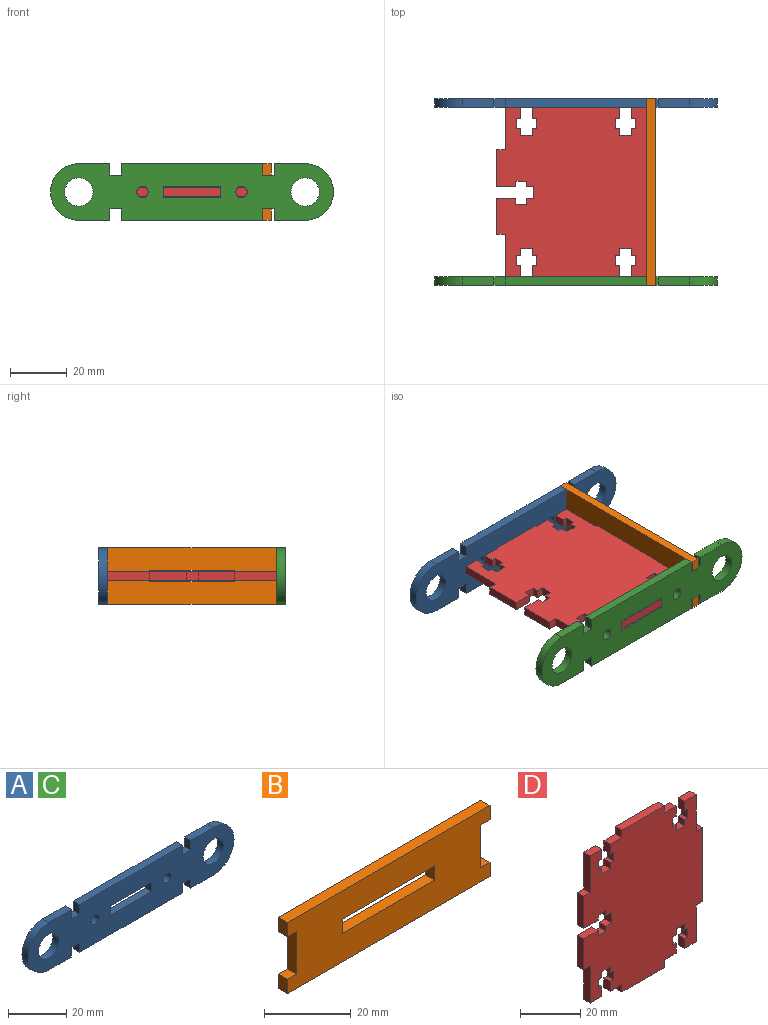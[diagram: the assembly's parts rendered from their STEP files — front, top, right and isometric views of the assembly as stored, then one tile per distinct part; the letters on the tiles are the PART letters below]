
ASSEMBLY  parts=4 mates=7
PART A: 30 faces, bbox 100x3x20 mm
  f0: cylinder r=10mm len=20mm, axis (0,1,0), area 94.2mm2, adj f1,f23,f28,f29
  f1: plane 11x3mm, normal (0,0,1), area 33mm2, adj f0,f2,f28,f29
  f2: plane 4x3mm, normal (-1,0,0), area 12mm2, adj f1,f3,f28,f29
  f3: plane 4x3mm, normal (0,0,1), area 12mm2, adj f2,f4,f28,f29
  f4: plane 4x3mm, normal (1,0,0), area 12mm2, adj f3,f5,f28,f29
  f5: plane 50x3mm, normal (0,0,1), area 150mm2, adj f4,f6,f28,f29
  f6: plane 4x3mm, normal (-1,0,0), area 12mm2, adj f5,f7,f28,f29
  f7: plane 4x3mm, normal (0,0,1), area 12mm2, adj f6,f8,f28,f29
  f8: plane 4x3mm, normal (1,0,0), area 12mm2, adj f7,f9,f28,f29
  f9: plane 11x3mm, normal (0,0,1), area 33mm2, adj f8,f10,f28,f29
  f10: cylinder r=10mm len=20mm, axis (0,1,0), area 94.2mm2, adj f9,f11,f28,f29
  f11: plane 11x3mm, normal (0,0,-1), area 33mm2, adj f10,f12,f28,f29
  f12: plane 4x3mm, normal (1,0,0), area 12mm2, adj f11,f13,f28,f29
  f13: plane 4x3mm, normal (0,0,-1), area 12mm2, adj f12,f14,f28,f29
  f14: plane 4x3mm, normal (-1,0,0), area 12mm2, adj f13,f15,f28,f29
  f15: plane 50x3mm, normal (0,0,-1), area 150mm2, adj f14,f16,f28,f29
  f16: plane 4x3mm, normal (1,0,0), area 12mm2, adj f15,f17,f28,f29
  f17: plane 4x3mm, normal (0,0,-1), area 12mm2, adj f16,f18,f28,f29
  f18: plane 4x3mm, normal (-1,0,0), area 12mm2, adj f17,f23,f28,f29
  f19: plane 20x3mm, normal (0,0,1), area 60mm2, adj f20,f24,f28,f29
  f20: plane 4x3mm, normal (1,0,0), area 12mm2, adj f19,f21,f28,f29
  f21: plane 20x3mm, normal (0,0,-1), area 60mm2, adj f20,f24,f28,f29
  f22: cylinder r=2mm len=4mm, axis (0,1,0), area 37.7mm2, adj f28,f29
  f23: plane 11x3mm, normal (0,0,-1), area 33mm2, adj f0,f18,f28,f29
  f24: plane 4x3mm, normal (-1,0,0), area 12mm2, adj f19,f21,f28,f29
  f25: cylinder r=5mm len=10mm, axis (0,1,0), area 94.2mm2, adj f28,f29
  f26: cylinder r=5mm len=10mm, axis (0,1,0), area 94.2mm2, adj f28,f29
  f27: cylinder r=2mm len=4mm, axis (0,1,0), area 37.7mm2, adj f28,f29
  f28: plane 100x20mm, normal (0,-1,0), area 1587.9mm2, adj f0,f1,f2,f3,f4,f5,f6,f7
  f29: plane 100x20mm, normal (0,1,0), area 1587.9mm2, adj f0,f1,f2,f3,f4,f5,f6,f7
PART B: 18 faces, bbox 66x3x20 mm
  f0: plane 3x3mm, normal (0,0,1), area 9mm2, adj f1,f15,f16,f17
  f1: plane 4x3mm, normal (-1,0,0), area 12mm2, adj f0,f2,f16,f17
  f2: plane 66x3mm, normal (0,0,-1), area 198mm2, adj f1,f3,f16,f17
  f3: plane 4x3mm, normal (1,0,0), area 12mm2, adj f2,f4,f16,f17
  f4: plane 3x3mm, normal (0,0,1), area 9mm2, adj f3,f5,f16,f17
  f5: plane 12x3mm, normal (1,0,0), area 36mm2, adj f4,f6,f16,f17
  f6: plane 3x3mm, normal (0,0,-1), area 9mm2, adj f5,f7,f16,f17
  f7: plane 4x3mm, normal (1,0,0), area 12mm2, adj f6,f8,f16,f17
  f8: plane 66x3mm, normal (0,0,1), area 198mm2, adj f7,f9,f16,f17
  f9: plane 4x3mm, normal (-1,0,0), area 12mm2, adj f8,f10,f16,f17
  f10: plane 3x3mm, normal (0,0,-1), area 9mm2, adj f9,f15,f16,f17
  f11: plane 30x3mm, normal (0,0,1), area 90mm2, adj f12,f14,f16,f17
  f12: plane 4x3mm, normal (1,0,0), area 12mm2, adj f11,f13,f16,f17
  f13: plane 30x3mm, normal (0,0,-1), area 90mm2, adj f12,f14,f16,f17
  f14: plane 4x3mm, normal (-1,0,0), area 12mm2, adj f11,f13,f16,f17
  f15: plane 12x3mm, normal (-1,0,0), area 36mm2, adj f0,f10,f16,f17
  f16: plane 66x20mm, normal (0,-1,0), area 1128mm2, adj f0,f1,f2,f3,f4,f5,f6,f7
  f17: plane 66x20mm, normal (0,1,0), area 1128mm2, adj f0,f1,f2,f3,f4,f5,f6,f7
PART C: same geometry as A
PART D: 82 faces, bbox 56x3x66 mm
  f0: plane 6.77x3mm, normal (0,0,1), area 20.3mm2, adj f1,f79,f80,f81
  f1: plane 12.64x3mm, normal (-1,0,0), area 37.9mm2, adj f0,f2,f80,f81
  f2: plane 3x3mm, normal (0,0,-1), area 9mm2, adj f1,f3,f80,f81
  f3: plane 15x3mm, normal (-1,0,0), area 45mm2, adj f2,f4,f80,f81
  f4: plane 5.5x3mm, normal (0,0,-1), area 16.5mm2, adj f3,f5,f80,f81
  f5: plane 4x3mm, normal (1,0,0), area 12mm2, adj f4,f6,f80,f81
  f6: plane 3x1.5mm, normal (0,0,1), area 4.5mm2, adj f5,f7,f80,f81
  f7: plane 3.5x3mm, normal (1,0,0), area 10.5mm2, adj f6,f8,f80,f81
  f8: plane 3x1.5mm, normal (0,0,-1), area 4.5mm2, adj f7,f9,f80,f81
  f9: plane 3x2.5mm, normal (1,0,0), area 7.5mm2, adj f8,f10,f80,f81
  f10: plane 4x3mm, normal (0,0,-1), area 12mm2, adj f9,f11,f80,f81
  f11: plane 3x2.5mm, normal (-1,0,0), area 7.5mm2, adj f10,f12,f80,f81
  f12: plane 3x1.5mm, normal (0,0,-1), area 4.5mm2, adj f11,f13,f80,f81
  f13: plane 3.5x3mm, normal (-1,0,0), area 10.5mm2, adj f12,f14,f80,f81
  f14: plane 3x1.5mm, normal (0,0,1), area 4.5mm2, adj f13,f15,f80,f81
  f15: plane 4x3mm, normal (-1,0,0), area 12mm2, adj f14,f16,f80,f81
  f16: plane 5.5x3mm, normal (0,0,-1), area 16.5mm2, adj f15,f17,f80,f81
  f17: plane 3x3mm, normal (-1,0,0), area 9mm2, adj f16,f18,f80,f81
  f18: plane 20x3mm, normal (0,0,-1), area 60mm2, adj f17,f19,f80,f81
  f19: plane 3x3mm, normal (1,0,0), area 9mm2, adj f18,f20,f80,f81
  f20: plane 5.5x3mm, normal (0,0,-1), area 16.5mm2, adj f19,f21,f80,f81
  f21: plane 4x3mm, normal (1,0,0), area 12mm2, adj f20,f22,f80,f81
  f22: plane 3x1.5mm, normal (0,0,1), area 4.5mm2, adj f21,f23,f80,f81
  f23: plane 3.5x3mm, normal (1,0,0), area 10.5mm2, adj f22,f24,f80,f81
  f24: plane 3x1.5mm, normal (0,0,-1), area 4.5mm2, adj f23,f25,f80,f81
  f25: plane 3x2.5mm, normal (1,0,0), area 7.5mm2, adj f24,f26,f80,f81
  f26: plane 4x3mm, normal (0,0,-1), area 12mm2, adj f25,f27,f80,f81
  f27: plane 3x2.5mm, normal (-1,0,0), area 7.5mm2, adj f26,f28,f80,f81
  f28: plane 3x1.5mm, normal (0,0,-1), area 4.5mm2, adj f27,f29,f80,f81
  f29: plane 3.5x3mm, normal (-1,0,0), area 10.5mm2, adj f28,f30,f80,f81
  f30: plane 3x1.5mm, normal (0,0,1), area 4.5mm2, adj f29,f31,f80,f81
  f31: plane 4x3mm, normal (-1,0,0), area 12mm2, adj f30,f32,f80,f81
  f32: plane 5.5x3mm, normal (0,0,-1), area 16.5mm2, adj f31,f33,f80,f81
  f33: plane 15x3mm, normal (1,0,0), area 45mm2, adj f32,f34,f80,f81
  f34: plane 3x3mm, normal (0,0,-1), area 9mm2, adj f33,f35,f80,f81
  f35: plane 30x3mm, normal (1,0,0), area 90mm2, adj f34,f36,f80,f81
  f36: plane 3x3mm, normal (0,0,1), area 9mm2, adj f35,f37,f80,f81
  f37: plane 15x3mm, normal (1,0,0), area 45mm2, adj f36,f38,f80,f81
  f38: plane 5.5x3mm, normal (0,0,1), area 16.5mm2, adj f37,f39,f80,f81
  f39: plane 4x3mm, normal (-1,0,0), area 12mm2, adj f38,f40,f80,f81
  f40: plane 3x1.5mm, normal (0,0,-1), area 4.5mm2, adj f39,f41,f80,f81
  f41: plane 3.5x3mm, normal (-1,0,0), area 10.5mm2, adj f40,f42,f80,f81
  f42: plane 3x1.5mm, normal (0,0,1), area 4.5mm2, adj f41,f43,f80,f81
  f43: plane 3x2.5mm, normal (-1,0,0), area 7.5mm2, adj f42,f44,f80,f81
  f44: plane 4x3mm, normal (0,0,1), area 12mm2, adj f43,f45,f80,f81
  f45: plane 3x2.5mm, normal (1,0,0), area 7.5mm2, adj f44,f46,f80,f81
  f46: plane 3x1.5mm, normal (0,0,1), area 4.5mm2, adj f45,f47,f80,f81
  f47: plane 3.5x3mm, normal (1,0,0), area 10.5mm2, adj f46,f48,f80,f81
  f48: plane 3x1.5mm, normal (0,0,-1), area 4.5mm2, adj f47,f49,f80,f81
  f49: plane 4x3mm, normal (1,0,0), area 12mm2, adj f48,f50,f80,f81
  f50: plane 5.5x3mm, normal (0,0,1), area 16.5mm2, adj f49,f51,f80,f81
  f51: plane 3x3mm, normal (1,0,0), area 9mm2, adj f50,f52,f80,f81
  f52: plane 20x3mm, normal (0,0,1), area 60mm2, adj f51,f53,f80,f81
  f53: plane 3x3mm, normal (-1,0,0), area 9mm2, adj f52,f54,f80,f81
  f54: plane 5.5x3mm, normal (0,0,1), area 16.5mm2, adj f53,f55,f80,f81
  f55: plane 4x3mm, normal (-1,0,0), area 12mm2, adj f54,f56,f80,f81
  f56: plane 3x1.5mm, normal (0,0,-1), area 4.5mm2, adj f55,f57,f80,f81
  f57: plane 3.5x3mm, normal (-1,0,0), area 10.5mm2, adj f56,f58,f80,f81
  f58: plane 3x1.5mm, normal (0,0,1), area 4.5mm2, adj f57,f59,f80,f81
  f59: plane 3x2.5mm, normal (-1,0,0), area 7.5mm2, adj f58,f60,f80,f81
  f60: plane 4x3mm, normal (0,0,1), area 12mm2, adj f59,f61,f80,f81
  f61: plane 3x2.5mm, normal (1,0,0), area 7.5mm2, adj f60,f62,f80,f81
  f62: plane 3x1.5mm, normal (0,0,1), area 4.5mm2, adj f61,f63,f80,f81
  f63: plane 3.5x3mm, normal (1,0,0), area 10.5mm2, adj f62,f64,f80,f81
  f64: plane 3x1.5mm, normal (0,0,-1), area 4.5mm2, adj f63,f65,f80,f81
  f65: plane 4x3mm, normal (1,0,0), area 12mm2, adj f64,f66,f80,f81
  f66: plane 5.5x3mm, normal (0,0,1), area 16.5mm2, adj f65,f67,f80,f81
  f67: plane 15x3mm, normal (-1,0,0), area 45mm2, adj f66,f68,f80,f81
  f68: plane 3x3mm, normal (0,0,1), area 9mm2, adj f67,f69,f80,f81
  f69: plane 13.14x3mm, normal (-1,0,0), area 39.4mm2, adj f68,f70,f80,f81
  f70: plane 6.77x3mm, normal (0,0,-1), area 20.3mm2, adj f69,f71,f80,f81
  f71: plane 3x2.02mm, normal (1,0,0), area 6.1mm2, adj f70,f72,f80,f81
  f72: plane 3.64x3mm, normal (0,0,-1), area 10.9mm2, adj f71,f73,f80,f81
  f73: plane 3x2.02mm, normal (-1,0,0), area 6.1mm2, adj f72,f74,f80,f81
  f74: plane 3x2.56mm, normal (0,0,-1), area 7.7mm2, adj f73,f75,f80,f81
  f75: plane 4.23x3mm, normal (-1,0,0), area 12.7mm2, adj f74,f76,f80,f81
  f76: plane 3x2.56mm, normal (0,0,1), area 7.7mm2, adj f75,f77,f80,f81
  f77: plane 3x2.05mm, normal (-1,0,0), area 6.2mm2, adj f76,f78,f80,f81
  f78: plane 3.64x3mm, normal (0,0,1), area 10.9mm2, adj f77,f79,f80,f81
  f79: plane 3x2.05mm, normal (1,0,0), area 6.2mm2, adj f0,f78,f80,f81
  f80: plane 66x56mm, normal (0,-1,0), area 3028.4mm2, adj f0,f1,f2,f3,f4,f5,f6,f7
  f81: plane 66x56mm, normal (0,1,0), area 3028.4mm2, adj f0,f1,f2,f3,f4,f5,f6,f7
PLACE A t=(-7.12,54.79,7.62)mm
PLACE B rot(axis=(0,0,-1),90deg) t=(20.88,21.79,7.62)mm
PLACE C t=(-7.12,-8.21,7.62)mm
PLACE D rot(axis=(-1,0,0),90deg) t=(-7.12,21.79,6.12)mm
MATE parallel C.f28 <-> A.f28  axis (0,-1,0) through (-7.12,-11.21,7.62)mm
MATE planar B.f16 <-> D.f37  axis (-1,0,0) through (17.88,21.79,7.62)mm
MATE planar D.f51 <-> A.f24  axis (1,0,0) through (2.88,53.29,7.62)mm
MATE planar C.f29 <-> D.f16  axis (0,1,0) through (-7.12,-8.21,7.62)mm
MATE planar D.f54 <-> A.f28  axis (0,1,0) through (-19.87,51.79,7.62)mm
MATE planar B.f15 <-> A.f28  axis (0,1,0) through (19.38,51.79,7.62)mm
MATE cylindrical A.f10 <-> C.f10  axis (0,1,0) through (-47.12,54.79,7.62)mm
